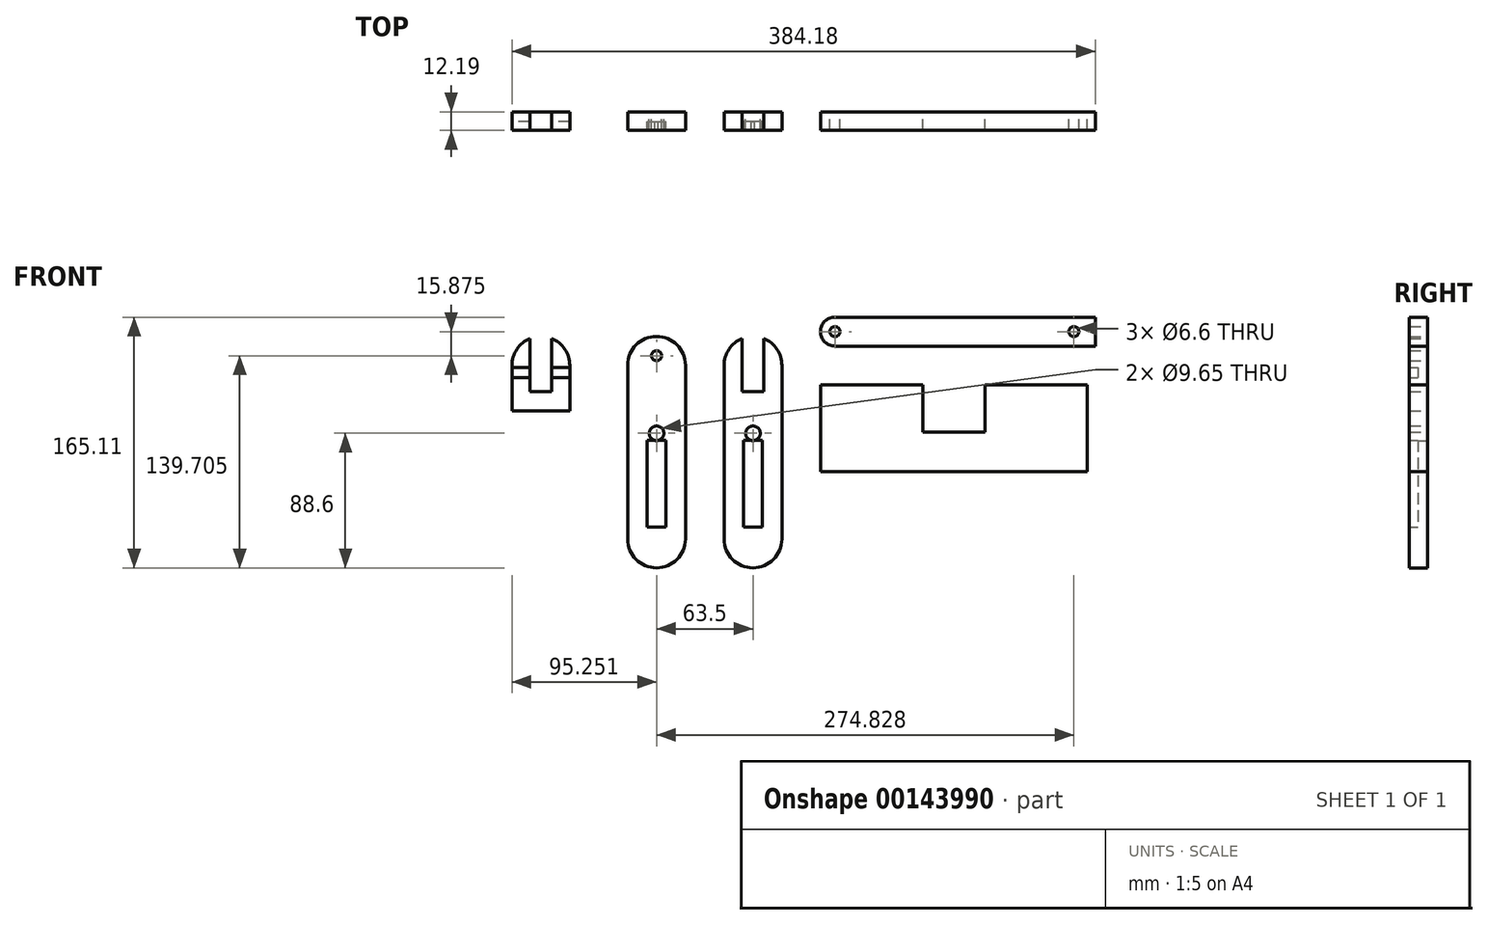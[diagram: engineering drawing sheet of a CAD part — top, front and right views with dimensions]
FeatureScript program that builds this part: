
annotation { "Feature Type Name" : "Feature", "Feature Type Description" : "" }
export const myFeature = defineFeature(function(context is Context, id is Id, definition is map)
    precondition{}
    {
        {
            var Q0;
            Q0=qCreatedBy(makeId("Front.planeOp"),FACE);
            var sketch = newSketch(context, id + "F0", { "sketchPlane" : qUnion([Q0])});
            skLineSegment(sketch, "E0.bottom", {"start": v(-87.86, 28.58) * mm, "end": v(87.86, 28.58) * mm});
            skLineSegment(sketch, "E0.top", {"start": v(-87.86, -28.58) * mm, "end": v(87.86, -28.58) * mm});
            skLineSegment(sketch, "E0.left", {"start": v(-87.86, 28.58) * mm, "end": v(-87.86, -28.58) * mm});
            skLineSegment(sketch, "E0.right", {"start": v(87.86, 28.58) * mm, "end": v(87.86, -28.58) * mm});
            skPoint(sketch, "E0.middle", {"position": v(0, 0) * mm});
            skLineSegment(sketch, "E1.bottom", {"start": v(-20.55, 28.57) * mm, "end": v(20.55, 28.58) * mm});
            skLineSegment(sketch, "E1.top", {"start": v(-20.55, -2.82) * mm, "end": v(20.55, -2.82) * mm});
            skLineSegment(sketch, "E1.left", {"start": v(-20.55, 28.58) * mm, "end": v(-20.55, -2.82) * mm});
            skLineSegment(sketch, "E1.right", {"start": v(20.55, 28.58) * mm, "end": v(20.55, -2.82) * mm});
            skPoint(sketch, "E2", {"position": v(0, -2.82) * mm});
            skLineSegment(sketch, "E3.bottom", {"start": v(-151.36, 60.32) * mm, "end": v(-113.26, 60.32) * mm});
            skLineSegment(sketch, "E3.top", {"start": v(-132.3, -92.08) * mm, "end": v(-132.3, -92.08) * mm});
            skLineSegment(sketch, "E3.left", {"start": v(-151.36, 60.32) * mm, "end": v(-151.36, -73.03) * mm});
            skLineSegment(sketch, "E3.right", {"start": v(-113.26, 60.32) * mm, "end": v(-113.26, -73.03) * mm});
            skLineSegment(sketch, "E4.bottom", {"start": v(-139.52, 60.32) * mm, "end": v(-125.1, 60.32) * mm});
            skLineSegment(sketch, "E4.top", {"start": v(-139.52, 23.95) * mm, "end": v(-125.1, 23.95) * mm});
            skLineSegment(sketch, "E4.left", {"start": v(-139.52, 60.32) * mm, "end": v(-139.52, 23.95) * mm});
            skLineSegment(sketch, "E4.right", {"start": v(-125.1, 60.32) * mm, "end": v(-125.1, 23.95) * mm});
            skPoint(sketch, "E4.middle", {"position": v(-132.3, 42.14) * mm});
            skPoint(sketch, "E4.middle.positionSnap0", {"position": v(-132.3, 60.32) * mm});
            skPoint(sketch, "E4.centerSnap0", {"position": v(-132.3, 60.32) * mm});
            skLineSegment(sketch, "E5", {"start": v(-151.36, -15.88) * mm, "end": v(-113.26, -15.88) * mm, "construction": true});
            skPoint(sketch, "E6.visualSharp", {"position": v(-151.36, -92.07) * mm});
            skArc(sketch, "E6.filletArc", {"start": v(-151.36, -73.03) * mm, "mid": v(-145.78, -86.5) * mm, "end": v(-132.3, -92.08) * mm});
            skPoint(sketch, "E7.visualSharp", {"position": v(-113.26, -92.07) * mm});
            skArc(sketch, "E7.filletArc", {"start": v(-132.3, -92.08) * mm, "mid": v(-118.84, -86.5) * mm, "end": v(-113.26, -73.03) * mm});
            skArc(sketch, "E8.MirrorCS", {"start": v(-151.36, 41.27) * mm, "mid": v(-145.78, 54.75) * mm, "end": v(-132.3, 60.33) * mm});
            skArc(sketch, "E9.MirrorCS", {"start": v(-132.3, 60.33) * mm, "mid": v(-118.84, 54.75) * mm, "end": v(-113.26, 41.27) * mm});
            skLineSegment(sketch, "E10.bottom", {"start": v(-126.21, -8.18) * mm, "end": v(-138.4, -8.18) * mm});
            skLineSegment(sketch, "E10.top", {"start": v(-126.21, -65.33) * mm, "end": v(-138.4, -65.33) * mm});
            skLineSegment(sketch, "E10.left", {"start": v(-126.21, -8.18) * mm, "end": v(-126.21, -65.33) * mm});
            skLineSegment(sketch, "E10.right", {"start": v(-138.4, -8.18) * mm, "end": v(-138.4, -65.33) * mm});
            skPoint(sketch, "E10.middle", {"position": v(-132.3, -36.75) * mm});
            skPoint(sketch, "E10.middle.positionSnap0", {"position": v(-132.3, 23.95) * mm});
            skPoint(sketch, "E10.centerSnap0", {"position": v(-132.3, 23.95) * mm});
            skCircle(sketch, "E11", {"center": v(-132.3, -3.48) * mm, "radius": 4.83 * mm});
            skPoint(sketch, "E11.centerSnap0", {"position": v(-132.3, -8.18) * mm});
            skLineSegment(sketch, "E12", {"start": v(-164.06, -92.08) * mm, "end": v(-164.06, 60.33) * mm, "construction": true});
            skArc(sketch, "E13.MirrorCS", {"start": v(-176.76, 41.27) * mm, "mid": v(-182.34, 54.75) * mm, "end": v(-195.8, 60.32) * mm});
            skArc(sketch, "E14.MirrorCS", {"start": v(-195.8, 60.33) * mm, "mid": v(-209.28, 54.75) * mm, "end": v(-214.86, 41.27) * mm});
            skLineSegment(sketch, "E15.MirrorCS", {"start": v(-214.86, 60.32) * mm, "end": v(-214.86, -73.03) * mm});
            skLineSegment(sketch, "E16.MirrorCS", {"start": v(-176.76, 60.32) * mm, "end": v(-176.76, -73.03) * mm});
            skArc(sketch, "E17.MirrorCS", {"start": v(-176.76, -73.03) * mm, "mid": v(-182.34, -86.5) * mm, "end": v(-195.8, -92.08) * mm});
            skArc(sketch, "E18.MirrorCS", {"start": v(-195.8, -92.08) * mm, "mid": v(-209.28, -86.5) * mm, "end": v(-214.86, -73.03) * mm});
            skCircle(sketch, "E19", {"center": v(-195.8, 47.62) * mm, "radius": 3.3 * mm});
            skCircle(sketch, "E20.MirrorC", {"center": v(-195.8, -3.48) * mm, "radius": 4.83 * mm});
            skLineSegment(sketch, "E21.MirrorCS", {"start": v(-201.9, -8.18) * mm, "end": v(-189.71, -8.18) * mm});
            skLineSegment(sketch, "E22.MirrorCS", {"start": v(-189.71, -8.18) * mm, "end": v(-189.71, -65.33) * mm});
            skLineSegment(sketch, "E23.MirrorCS", {"start": v(-201.9, -8.18) * mm, "end": v(-201.9, -65.33) * mm});
            skLineSegment(sketch, "E24.MirrorCS", {"start": v(-201.9, -65.33) * mm, "end": v(-189.71, -65.33) * mm});
            skLineSegment(sketch, "E25.bottom", {"start": v(-78.33, 53.98) * mm, "end": v(93.12, 53.98) * mm});
            skLineSegment(sketch, "E25.top", {"start": v(-78.33, 73.03) * mm, "end": v(93.12, 73.03) * mm});
            skLineSegment(sketch, "E25.left", {"start": v(-87.86, 63.5) * mm, "end": v(-87.86, 63.5) * mm});
            skLineSegment(sketch, "E25.right", {"start": v(93.12, 53.98) * mm, "end": v(93.12, 73.03) * mm});
            skPoint(sketch, "E26.visualSharp", {"position": v(-87.86, 73.03) * mm});
            skArc(sketch, "E26.filletArc", {"start": v(-78.33, 73.03) * mm, "mid": v(-85.07, 70.24) * mm, "end": v(-87.86, 63.5) * mm});
            skPoint(sketch, "E27.visualSharp", {"position": v(-87.86, 53.98) * mm});
            skArc(sketch, "E27.filletArc", {"start": v(-87.86, 63.5) * mm, "mid": v(-85.07, 56.76) * mm, "end": v(-78.33, 53.98) * mm});
            skCircle(sketch, "E28", {"center": v(79.02, 63.5) * mm, "radius": 3.3 * mm});
            skPoint(sketch, "E28.centerSnap0", {"position": v(93.12, 63.5) * mm});
            skArc(sketch, "E29.MirrorCS", {"start": v(-233.9, 60.33) * mm, "mid": v(-220.44, 54.75) * mm, "end": v(-214.86, 41.27) * mm, "construction": true});
            skArc(sketch, "E30.MirrorCS", {"start": v(-252.96, 41.27) * mm, "mid": v(-247.38, 54.75) * mm, "end": v(-233.9, 60.32) * mm, "construction": true});
            skLineSegment(sketch, "E31", {"start": v(-252.96, 41.27) * mm, "end": v(-252.96, 11.25) * mm});
            skLineSegment(sketch, "E32", {"start": v(-252.96, 11.25) * mm, "end": v(-214.86, 11.25) * mm, "construction": true});
            skLineSegment(sketch, "E33", {"start": v(-252.96, 33.21) * mm, "end": v(-214.86, 33.21) * mm, "construction": true});
            skLineSegment(sketch, "E34", {"start": v(-252.96, 39.81) * mm, "end": v(-214.86, 39.81) * mm, "construction": true});
            skLineSegment(sketch, "E35", {"start": v(-233.9, 39.81) * mm, "end": v(-233.9, 33.21) * mm, "construction": true});
            skPoint(sketch, "E36", {"position": v(-233.9, 36.51) * mm});
            skLineSegment(sketch, "E37", {"start": v(-233.9, 73.02) * mm, "end": v(-132.3, 73.02) * mm, "construction": true});
            skLineSegment(sketch, "E38", {"start": v(-183.1, 73.02) * mm, "end": v(-183.1, 98.42) * mm, "construction": true});
            skLineSegment(sketch, "E39.MirrorCS", {"start": v(-226.7, 60.32) * mm, "end": v(-226.7, 23.95) * mm, "construction": true});
            skLineSegment(sketch, "E40.MirrorCS", {"start": v(-241.12, 60.32) * mm, "end": v(-241.12, 23.95) * mm, "construction": true});
            skLineSegment(sketch, "E41.MirrorCS", {"start": v(-226.7, 23.95) * mm, "end": v(-241.12, 23.95) * mm, "construction": true});
            skLineSegment(sketch, "E42.MirrorCS", {"start": v(-272, 39.81) * mm, "end": v(-272, 33.21) * mm});
            skLineSegment(sketch, "E43.MirrorCS", {"start": v(-252.96, 11.25) * mm, "end": v(-291.06, 11.25) * mm});
            skLineSegment(sketch, "E44.MirrorCS", {"start": v(-264.8, 60.32) * mm, "end": v(-264.8, 23.95) * mm});
            skPoint(sketch, "E45.MirrorP", {"position": v(-272, 36.51) * mm});
            skLineSegment(sketch, "E46.MirrorCS", {"start": v(-252.96, 39.81) * mm, "end": v(-291.06, 39.81) * mm});
            skLineSegment(sketch, "E47.MirrorCS", {"start": v(-279.22, 23.95) * mm, "end": v(-264.8, 23.95) * mm});
            skArc(sketch, "E48.MirrorCS", {"start": v(-252.96, 41.27) * mm, "mid": v(-258.54, 54.75) * mm, "end": v(-272, 60.32) * mm});
            skLineSegment(sketch, "E49.MirrorCS", {"start": v(-252.96, 33.21) * mm, "end": v(-291.06, 33.21) * mm});
            skArc(sketch, "E50.MirrorCS", {"start": v(-272, 60.33) * mm, "mid": v(-285.48, 54.75) * mm, "end": v(-291.06, 41.27) * mm});
            skLineSegment(sketch, "E51.MirrorCS", {"start": v(-279.22, 60.32) * mm, "end": v(-279.22, 23.95) * mm});
            skLineSegment(sketch, "E52", {"start": v(-291.06, 41.27) * mm, "end": v(-291.06, 11.25) * mm});
            skCircle(sketch, "E53", {"center": v(-78.33, 63.5) * mm, "radius": 3.3 * mm});
            skSolve(sketch);
        }
        {
            var Q0;
            Q0=makeQuery(id+"F0.imprint","IMPRINT",FACE,{"disambiguationData":[TD([[makeQuery(id+"F0.imprint","IMPRINT",EDGE,{"derivedFrom":sQuery(id+"F0.wireOp",EDGE,"E25.bottom")}),1.0]])]});
            var Q1;
            Q1=makeQuery(id+"F0.imprint","IMPRINT",FACE,{"disambiguationData":[TD([[makeQuery(id+"F0.imprint","IMPRINT",EDGE,{"derivedFrom":sQuery(id+"F0.wireOp",EDGE,"E0.top")}),1.0]])]});
            var Q2;
            {var subQ5=sQuery(id+"F0.wireOp",EDGE,"E32");Q2=makeQuery(id+"F0.imprint","IMPRINT",FACE,{"disambiguationData":[TD([[makeQuery(id+"F0.imprint","IMPRINT",EDGE,{"derivedFrom":subQ5}),1.0]])]});}
            var Q3;
            {var subQ1=sQuery(id+"F0.wireOp",EDGE,"E15.MirrorCS");var subQ3=sQuery(id+"F0.wireOp",EDGE,"E34");var subQ4=makeQuery(id+"F0.imprint","INTERSECT",VERTEX,{"derivedFrom":[subQ1,subQ3]});Q3=makeQuery(id+"F0.imprint","IMPRINT",FACE,{"disambiguationData":[TD([[makeQuery(id+"F0.imprint","IMPRINT",EDGE,{"disambiguationData":[TD([[subQ4,1.0]])],"derivedFrom":subQ3}),1.0]])]});}
            var Q4;
            {var subQ0=sQuery(id+"F0.wireOp",EDGE,"E31");var subQ1=sQuery(id+"F0.wireOp",EDGE,"E30.MirrorCS");var subQ2=makeQuery(id+"F0.imprint","INTERSECT",VERTEX,{"derivedFrom":[subQ1,subQ0]});Q4=makeQuery(id+"F0.imprint","IMPRINT",FACE,{"disambiguationData":[TD([[makeQuery(id+"F0.imprint","IMPRINT",EDGE,{"disambiguationData":[TD([[subQ2,-1.0]])],"derivedFrom":subQ1}),-1.0]])]});}
            var Q5;
            {var subQ3=sQuery(id+"F0.wireOp",EDGE,"E13.MirrorCS");Q5=makeQuery(id+"F0.imprint","IMPRINT",FACE,{"disambiguationData":[TD([[makeQuery(id+"F0.imprint","IMPRINT",EDGE,{"derivedFrom":subQ3}),1.0]])]});}
            var Q6;
            {var subQ8=sQuery(id+"F0.wireOp",EDGE,"E43.MirrorCS");Q6=makeQuery(id+"F0.imprint","IMPRINT",FACE,{"disambiguationData":[TD([[makeQuery(id+"F0.imprint","IMPRINT",EDGE,{"derivedFrom":subQ8}),-1.0]])]});}
            var Q7;
            {var subQ12=sQuery(id+"F0.wireOp",EDGE,"E4.top");Q7=makeQuery(id+"F0.imprint","IMPRINT",FACE,{"disambiguationData":[TD([[makeQuery(id+"F0.imprint","IMPRINT",EDGE,{"derivedFrom":subQ12}),-1.0]])]});}
            var Q8;
            {var subQ0=sQuery(id+"F0.wireOp",EDGE,"E48.MirrorCS");var subQ1=sQuery(id+"F0.wireOp",EDGE,"E31");var subQ2=makeQuery(id+"F0.imprint","INTERSECT",VERTEX,{"derivedFrom":[subQ1,subQ0]});Q8=makeQuery(id+"F0.imprint","IMPRINT",FACE,{"disambiguationData":[TD([[makeQuery(id+"F0.imprint","IMPRINT",EDGE,{"disambiguationData":[TD([[subQ2,-1.0]])],"derivedFrom":subQ1}),-1.0]])]});}
            var Q9;
            {var subQ0=sQuery(id+"F0.wireOp",EDGE,"E52");var subQ1=sQuery(id+"F0.wireOp",EDGE,"E46.MirrorCS");var subQ2=makeQuery(id+"F0.imprint","INTERSECT",VERTEX,{"derivedFrom":[subQ1,subQ0]});Q9=makeQuery(id+"F0.imprint","IMPRINT",FACE,{"disambiguationData":[TD([[makeQuery(id+"F0.imprint","IMPRINT",EDGE,{"disambiguationData":[TD([[subQ2,1.0]])],"derivedFrom":subQ1}),-1.0]])]});}
            extrude(context, id + "F1", {"entities" : qUnion([Q0, Q1, Q2, Q3, Q4, Q5, Q6, Q7, Q8, Q9]), "depth" : 12.2 * mm});
        }
        {
            var Q0;
            {var subQ0=sQuery(id+"F0.wireOp",EDGE,"E33");var subQ1=sQuery(id+"F0.wireOp",EDGE,"E31");var subQ2=makeQuery(id+"F0.imprint","INTERSECT",VERTEX,{"derivedFrom":[subQ1,subQ0]});Q0=makeQuery(id+"F0.imprint","IMPRINT",FACE,{"disambiguationData":[TD([[makeQuery(id+"F0.imprint","IMPRINT",EDGE,{"disambiguationData":[TD([[subQ2,1.0]])],"derivedFrom":subQ1}),1.0]])]});}
            var Q1;
            {var subQ0=sQuery(id+"F0.wireOp",EDGE,"E33");var subQ1=sQuery(id+"F0.wireOp",EDGE,"E15.MirrorCS");var subQ2=makeQuery(id+"F0.imprint","INTERSECT",VERTEX,{"derivedFrom":[subQ1,subQ0]});Q1=makeQuery(id+"F0.imprint","IMPRINT",FACE,{"disambiguationData":[TD([[makeQuery(id+"F0.imprint","IMPRINT",EDGE,{"disambiguationData":[TD([[subQ2,1.0]])],"derivedFrom":subQ1}),-1.0]])]});}
            var Q2;
            {var subQ0=sQuery(id+"F0.wireOp",EDGE,"E22.MirrorCS");Q2=makeQuery(id+"F0.imprint","IMPRINT",FACE,{"disambiguationData":[TD([[makeQuery(id+"F0.imprint","IMPRINT",EDGE,{"derivedFrom":subQ0}),-1.0]])]});}
            var Q3;
            Q3=makeQuery(id+"F0.imprint","IMPRINT",FACE,{"disambiguationData":[TD([[makeQuery(id+"F0.imprint","IMPRINT",EDGE,{"derivedFrom":sQuery(id+"F0.wireOp",EDGE,"E10.top")}),-1.0]])]});
            var Q4;
            {var subQ0=sQuery(id+"F0.wireOp",EDGE,"E52");var subQ1=sQuery(id+"F0.wireOp",EDGE,"E46.MirrorCS");var subQ2=makeQuery(id+"F0.imprint","INTERSECT",VERTEX,{"derivedFrom":[subQ1,subQ0]});Q4=makeQuery(id+"F0.imprint","IMPRINT",FACE,{"disambiguationData":[TD([[makeQuery(id+"F0.imprint","IMPRINT",EDGE,{"disambiguationData":[TD([[subQ2,1.0]])],"derivedFrom":subQ1}),1.0]])]});}
            var Q5;
            {var subQ0=sQuery(id+"F0.wireOp",EDGE,"E46.MirrorCS");var subQ1=sQuery(id+"F0.wireOp",EDGE,"E31");var subQ2=makeQuery(id+"F0.imprint","INTERSECT",VERTEX,{"derivedFrom":[subQ1,subQ0]});Q5=makeQuery(id+"F0.imprint","IMPRINT",FACE,{"disambiguationData":[TD([[makeQuery(id+"F0.imprint","IMPRINT",EDGE,{"disambiguationData":[TD([[subQ2,-1.0]])],"derivedFrom":subQ1}),-1.0]])]});}
            extrude(context, id + "F2", {"entities" : qUnion([Q0, Q1, Q2, Q3, Q4, Q5]), "operationType" : NewBodyOperationType.ADD, "depth" : 6.35 * mm});
        }
    });
